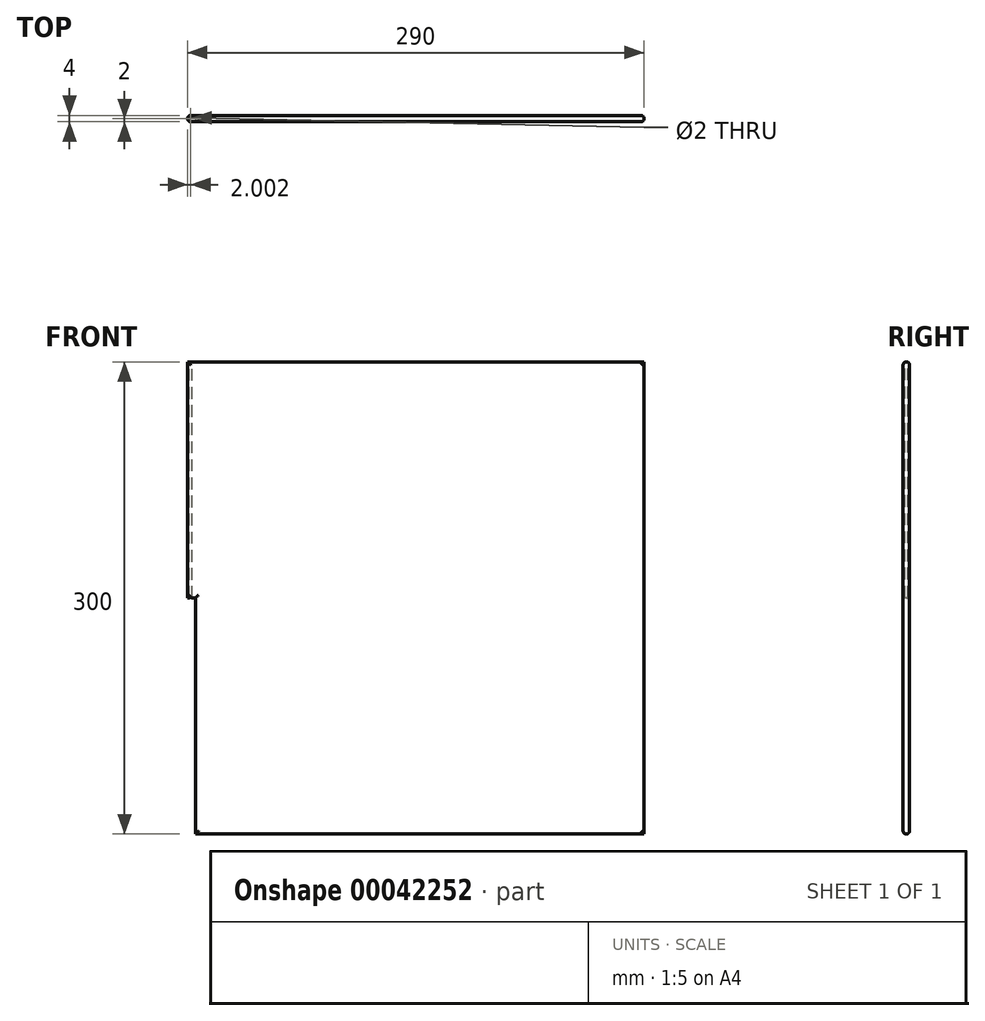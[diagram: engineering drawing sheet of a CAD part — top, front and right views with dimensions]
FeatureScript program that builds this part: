
annotation { "Feature Type Name" : "Feature", "Feature Type Description" : "" }
export const myFeature = defineFeature(function(context is Context, id is Id, definition is map)
    precondition{}
    {
        {
            var Q0;
            Q0=qCreatedBy(makeId("Front.planeOp"),FACE);
            var sketch = newSketch(context, id + "F0", { "sketchPlane" : qUnion([Q0])});
            skLineSegment(sketch, "E0.bottom", {"start": v(-38.59, 250.85) * mm, "end": v(251.41, 250.85) * mm});
            skLineSegment(sketch, "E0.right", {"start": v(251.41, 250.85) * mm, "end": v(251.41, -49.15) * mm});
            skLineSegment(sketch, "E1", {"start": v(-38.59, 250.85) * mm, "end": v(-38.59, 100.85) * mm});
            skLineSegment(sketch, "E2", {"start": v(-38.59, 100.85) * mm, "end": v(-33.59, 100.85) * mm});
            skLineSegment(sketch, "E3", {"start": v(-33.59, 100.85) * mm, "end": v(-33.59, -49.15) * mm});
            skLineSegment(sketch, "E4", {"start": v(-33.59, -49.15) * mm, "end": v(251.41, -49.15) * mm});
            skSolve(sketch);
        }
        {
            var Q0;
            Q0 = qSketchRegion(id + "F0", true);
            extrude(context, id + "F1", {"entities" : qUnion([Q0]), "depth" : 4 * mm});
        }
        {
            var Q0;
            Q0=makeQuery(id+"F1.opExtrude","SWEPT_FACE",FACE,{"disambiguationData":[OSD([sQuery(id+"F0.wireOp",EDGE,"E0.bottom")])]});
            var sketch = newSketch(context, id + "F2", { "sketchPlane" : qUnion([Q0])});
            skLineSegment(sketch, "E5", {"start": v(-38.59, 0) * mm, "end": v(-34.59, 0) * mm, "construction": true});
            skLineSegment(sketch, "E6", {"start": v(-34.59, 0) * mm, "end": v(-34.59, -4) * mm, "construction": true});
            skLineSegment(sketch, "E7", {"start": v(-38.59, -4) * mm, "end": v(-34.59, 0) * mm, "construction": true});
            skCircle(sketch, "E8", {"center": v(-36.59, -2) * mm, "radius": 1 * mm});
            skSolve(sketch);
        }
        {
            var Q0;
            Q0 = qSketchRegion(id + "F2", true);
            extrude(context, id + "F3", {"entities" : qUnion([Q0]), "operationType" : NewBodyOperationType.REMOVE, "oppositeDirection" : true, "depth" : 310 * mm});
        }
        {
            var Q0;
            Q0=makeQuery(id+"F1.opExtrude","CAP_FACE",FACE,{"disambiguationData":[OSD([sQuery(id+"F0.wireOp",EDGE,"E0.bottom"),sQuery(id+"F0.wireOp",EDGE,"E0.top"),sQuery(id+"F0.wireOp",EDGE,"E0.left"),sQuery(id+"F0.wireOp",EDGE,"E0.right")])],"isStart":false});
            fillet(context, id + "F4", {"entities" : qUnion([Q0]), "radius" : 2 * mm, "tangentPropagation" : true, "allowEdgeOverflow" : false});
        }
        {
            var Q0;
            Q0=makeQuery(id+"F1.opExtrude","CAP_FACE",FACE,{"disambiguationData":[OSD([sQuery(id+"F0.wireOp",EDGE,"E0.bottom"),sQuery(id+"F0.wireOp",EDGE,"E0.top"),sQuery(id+"F0.wireOp",EDGE,"E0.left"),sQuery(id+"F0.wireOp",EDGE,"E0.right")])],"isStart":true});
            fillet(context, id + "F5", {"entities" : qUnion([Q0]), "radius" : 2 * mm, "tangentPropagation" : true, "allowEdgeOverflow" : false});
        }
    });
